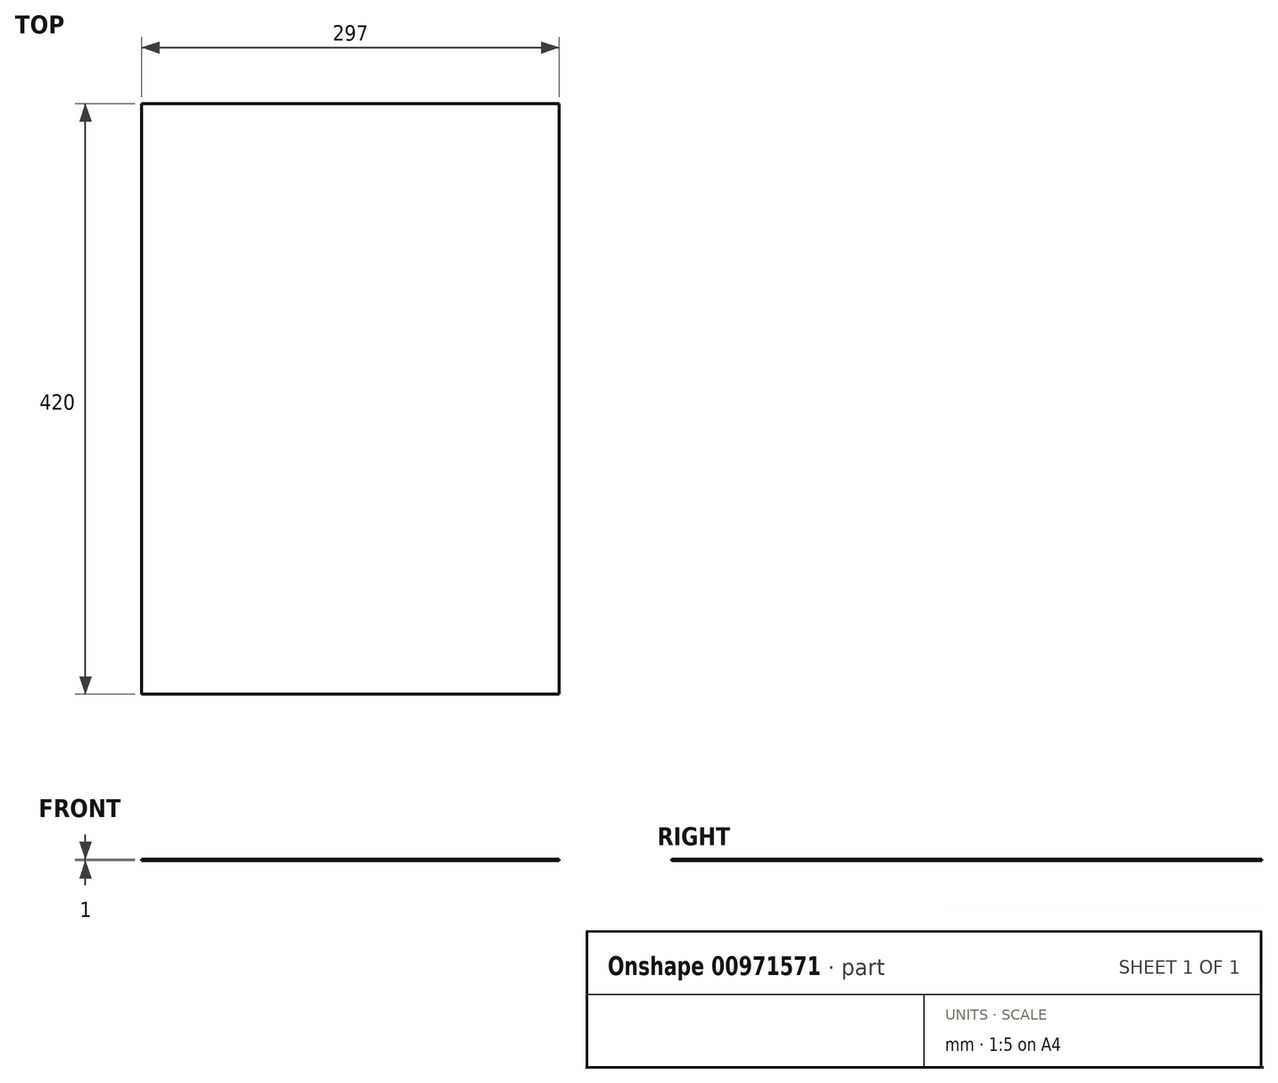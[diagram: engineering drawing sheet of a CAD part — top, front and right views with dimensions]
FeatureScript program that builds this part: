
annotation { "Feature Type Name" : "Feature", "Feature Type Description" : "" }
export const myFeature = defineFeature(function(context is Context, id is Id, definition is map)
    precondition{}
    {
        {
            var Q0;
            Q0=qCreatedBy(makeId("Top.planeOp"),FACE);
            var sketch = newSketch(context, id + "F0", { "sketchPlane" : qUnion([Q0])});
            skLineSegment(sketch, "E0.bottom", {"start": v(-159.84, 211.62) * mm, "end": v(137.16, 211.62) * mm});
            skLineSegment(sketch, "E0.top", {"start": v(-159.84, -208.38) * mm, "end": v(137.16, -208.38) * mm});
            skLineSegment(sketch, "E0.left", {"start": v(-159.84, 211.62) * mm, "end": v(-159.84, -208.38) * mm});
            skLineSegment(sketch, "E0.right", {"start": v(137.16, 211.62) * mm, "end": v(137.16, -208.38) * mm});
            skSolve(sketch);
        }
        {
            var Q0;
            Q0=makeQuery(id+"F0.imprint","IMPRINT",FACE,{"disambiguationData":[TD([[makeQuery(id+"F0.imprint","IMPRINT",EDGE,{"derivedFrom":sQuery(id+"F0.wireOp",EDGE,"E0.bottom")}),-1.0]])]});
            extrude(context, id + "F1", {"entities" : qUnion([Q0]), "depth" : 1 * mm, "offsetDistance" : 25 * mm});
        }
    });
